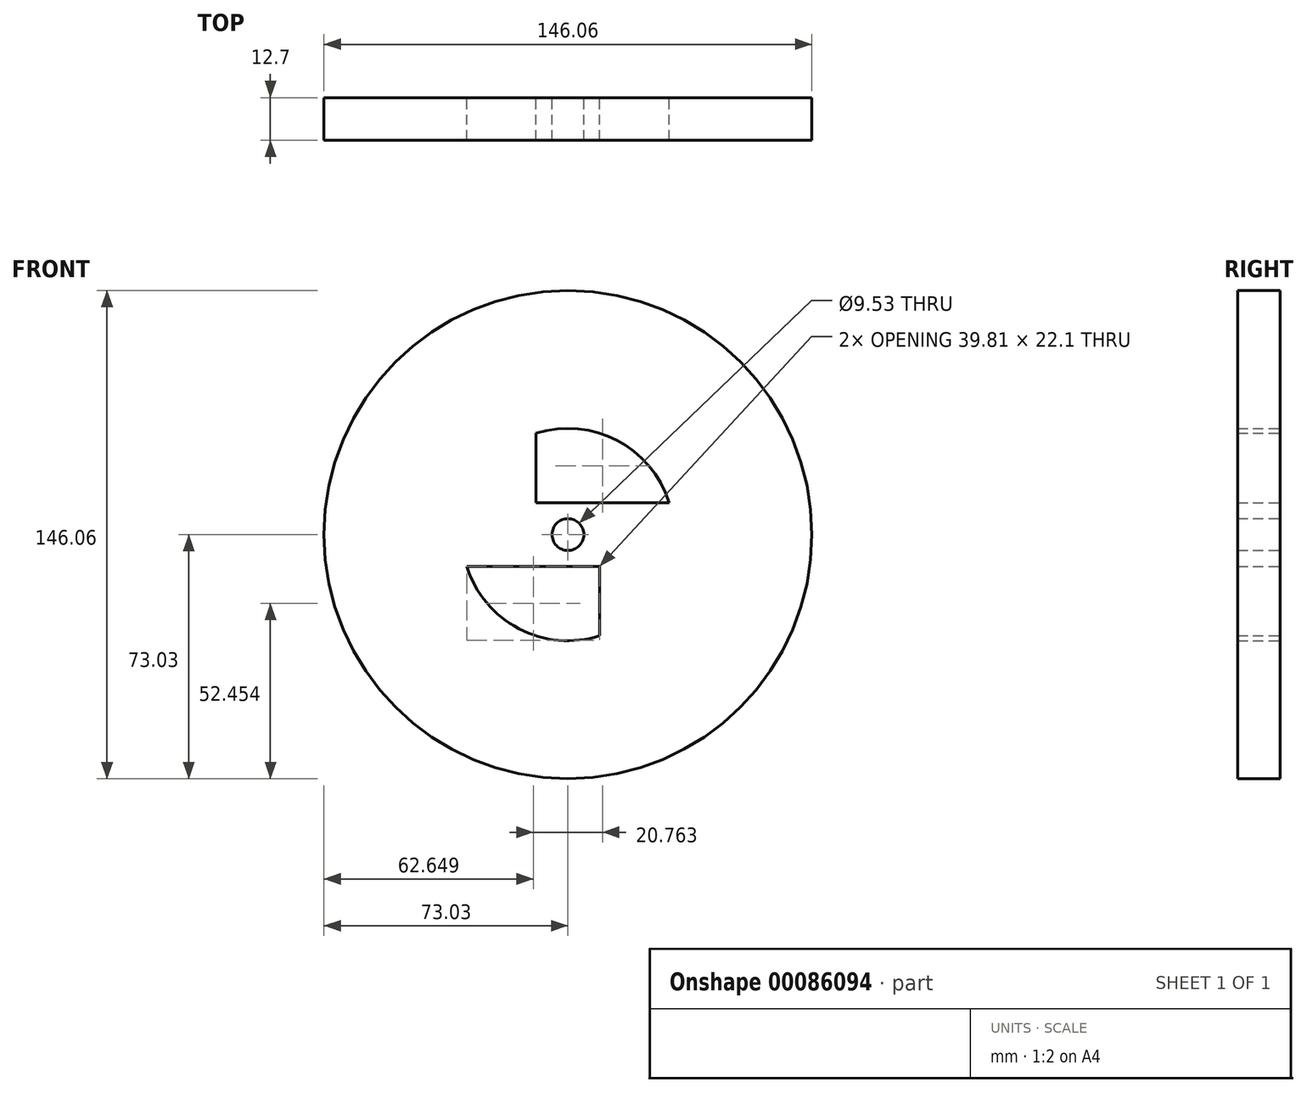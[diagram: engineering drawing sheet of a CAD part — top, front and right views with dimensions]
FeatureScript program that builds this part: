
annotation { "Feature Type Name" : "Feature", "Feature Type Description" : "" }
export const myFeature = defineFeature(function(context is Context, id is Id, definition is map)
    precondition{}
    {
        {
            var Q0;
            Q0=qCreatedBy(makeId("Front.planeOp"),FACE);
            var sketch = newSketch(context, id + "F0", { "sketchPlane" : qUnion([Q0])});
            skCircle(sketch, "E0", {"center": v(0, 0) * mm, "radius": 73.03 * mm});
            skCircle(sketch, "E1", {"center": v(0, 0) * mm, "radius": 4.76 * mm});
            skCircle(sketch, "E2", {"center": v(0, 0) * mm, "radius": 31.75 * mm});
            skLineSegment(sketch, "E3", {"start": v(0, 73.03) * mm, "end": v(0, -73.03) * mm, "construction": true});
            skLineSegment(sketch, "E4", {"start": v(-73.03, 0) * mm, "end": v(73.03, 0) * mm, "construction": true});
            skLineSegment(sketch, "E5", {"start": v(-9.53, 72.4) * mm, "end": v(-9.52, -72.4) * mm});
            skLineSegment(sketch, "E6", {"start": v(-72.4, 9.53) * mm, "end": v(72.4, 9.53) * mm});
            skLineSegment(sketch, "E7.MirrorCS", {"start": v(-72.4, -9.53) * mm, "end": v(72.4, -9.53) * mm});
            skLineSegment(sketch, "E8.MirrorCS", {"start": v(9.53, 72.4) * mm, "end": v(9.52, -72.4) * mm});
            skSolve(sketch);
        }
        {
            var Q0;
            Q0 = qSketchRegion(id + "F0", true);
            var Q1;
            {var subQ0=sQuery(id+"F0.wireOp",EDGE,"E6");var subQ1=sQuery(id+"F0.wireOp",EDGE,"E2");var subQ2=makeQuery(id+"F0.imprint","INTERSECT",VERTEX,{"disambiguationData":[OD(0.0)],"derivedFrom":[subQ1,subQ0]});Q1=makeQuery(id+"F0.imprint","IMPRINT",FACE,{"disambiguationData":[TD([[makeQuery(id+"F0.imprint","IMPRINT",EDGE,{"disambiguationData":[TD([[subQ2,1.0]])],"derivedFrom":subQ1}),1.0]])]});}
            var Q2;
            {var subQ0=sQuery(id+"F0.wireOp",EDGE,"E8.MirrorCS");var subQ1=sQuery(id+"F0.wireOp",EDGE,"E2");var subQ2=makeQuery(id+"F0.imprint","INTERSECT",VERTEX,{"disambiguationData":[OD(0.0)],"derivedFrom":[subQ1,subQ0]});Q2=makeQuery(id+"F0.imprint","IMPRINT",FACE,{"disambiguationData":[TD([[makeQuery(id+"F0.imprint","IMPRINT",EDGE,{"disambiguationData":[TD([[subQ2,-1.0]])],"derivedFrom":subQ1}),1.0]])]});}
            var Q3;
            {var subQ0=sQuery(id+"F0.wireOp",EDGE,"E6");var subQ1=sQuery(id+"F0.wireOp",EDGE,"E2");var subQ2=makeQuery(id+"F0.imprint","INTERSECT",VERTEX,{"disambiguationData":[OD(1.0)],"derivedFrom":[subQ1,subQ0]});Q3=makeQuery(id+"F0.imprint","IMPRINT",FACE,{"disambiguationData":[TD([[makeQuery(id+"F0.imprint","IMPRINT",EDGE,{"disambiguationData":[TD([[subQ2,-1.0]])],"derivedFrom":subQ1}),1.0]])]});}
            var Q4;
            Q4=makeQuery(id+"F0.imprint","IMPRINT",FACE,{"disambiguationData":[TD([[makeQuery(id+"F0.imprint","IMPRINT",EDGE,{"derivedFrom":sQuery(id+"F0.wireOp",EDGE,"E1")}),-1.0]])]});
            var Q5;
            {var subQ0=sQuery(id+"F0.wireOp",EDGE,"E5");var subQ1=sQuery(id+"F0.wireOp",EDGE,"E2");var subQ2=makeQuery(id+"F0.imprint","INTERSECT",VERTEX,{"disambiguationData":[OD(1.0)],"derivedFrom":[subQ1,subQ0]});Q5=makeQuery(id+"F0.imprint","IMPRINT",FACE,{"disambiguationData":[TD([[makeQuery(id+"F0.imprint","IMPRINT",EDGE,{"disambiguationData":[TD([[subQ2,-1.0]])],"derivedFrom":subQ1}),1.0]])]});}
            extrude(context, id + "F1", {"entities" : qUnion([Q0, Q1, Q2, Q3, Q4, Q5]), "depth" : 12.7 * mm});
        }
    });
